# Revit family: ARKOSLIGHT_Yoru
name_source: partatom
category: Lighting Fixtures
units: mm (PartAtom-declared; Revit-internal decimal feet)

## family parameters
Always vertical = Yes
Cut with Voids When Loaded = No
Light Source = No
OmniClass Number = 23.80.70.00
OmniClass Title = Lighting
Part Type = Normal
Room Calculation Point = No
Round Connector Dimension = Use Diameter
Shared = No
Work Plane-Based = No

## types (2) — shared parameters
ARKOSLIGHT_Apparent Load = 3 VA
ARKOSLIGHT_Beam Angle = 100.00°
ARKOSLIGHT_CCT = 2700 K
ARKOSLIGHT_CRI = CRI>90
ARKOSLIGHT_Dimming = 3-STEP DIMMING 100% - 50% - 10% - 0% (Switch off)
ARKOSLIGHT_Efficiency = 84%
ARKOSLIGHT_Fixture Type = WALL, FLOOR & PORTABLE
ARKOSLIGHT_IES = A456-00-00 YORU 2700K CRI90.ies
ARKOSLIGHT_IP = 20
ARKOSLIGHT_Luminous flux = 400 lm
ARKOSLIGHT_Model = YORU
ARKOSLIGHT_Series = YORU
Apparent Load = 3 VA
Manufacturer = ARKOSLIGHT
Model = YORU
URL = https://www.arkoslight.com

## per-type parameters (varying)
| type | ARKOSLIGHT_Body Color | ARKOSLIGHT_Color | ARKOSLIGHT_Reference | IES |
| A4560000WT - YORU 2700K WT | ARKOSLIGHT_Textured white | Textured white | A4560000WT | IES : A4560000WT - YORU 2700K WT |
| A4560000NT - YORU 2700K NT | ARKOSLIGHT_Textured black | Textured black | A4560000NT | IES : A4560000NT - YORU 2700K NT |

## geometry (parser evidence)
native form markers: Sweep x5
no freeform markers — native parametric forms only
